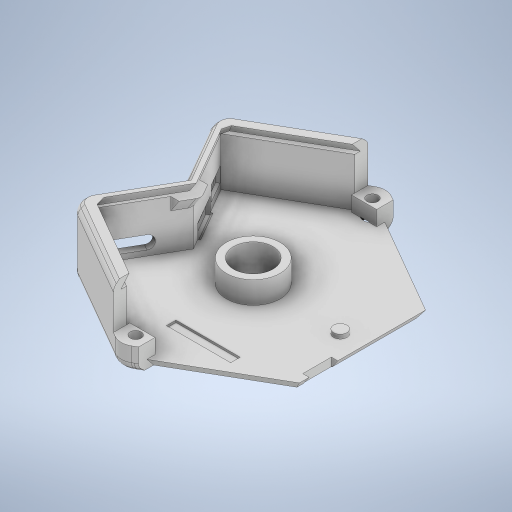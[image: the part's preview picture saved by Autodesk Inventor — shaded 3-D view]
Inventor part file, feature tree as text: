
AUTODESK INVENTOR PART (.ipt)
format: ipt  version: 2024 (Build 280153000, 153)  size: 1,035,776 bytes
history: native  units: in
note: dims shown in document units (in); Inventor stores cm internally (conversion verified against a paired STEP export)
features: extrude x31, move_body x17, direct_edit x9, draft x6, sketch x4, fillet x3, chamfer x3, plane x1
ambient origin geometry x8: Origin, YZ Plane, XZ Plane, XY Plane, X Axis, Y Axis, Z Axis, Center Point
bodies: Solid1 (feature_tree)
feature tree (74):
  extrude  "Extrusion1"  Depth=0.374in
  extrude  "Extrusion2"  Depth=0.0787in TaperAngle=0.0deg
  extrude  "Extrusion3"  Depth=0.6181in TaperAngle=0.0deg
  extrude  "Extrusion6"  Depth=0.0197in
  extrude  "Extrusion9"  Depth=0.0197in
  extrude  "Extrusion11"  Depth=0.0197in
  extrude  "Extrusion12"  Depth=0.0197in
  extrude  "Extrusion13"  TaperAngle=0.0deg  [1 undecoded]
  extrude  "Extrusion14"  Depth=0.0197in
  extrude  "Extrusion15"  Depth=0.0197in
  extrude  "Extrusion16"  Depth=0.0709in
  direct_edit  "Direct Edit2"
  direct_edit  "Direct Edit3"
  extrude  "Extrusion17"  Depth=0.0709in
  extrude  "Extrusion19"  Depth=0.0197in
  extrude  "Extrusion26"  Depth=0.0197in
  extrude  "Extrusion27"  TaperAngle=0.0deg  [1 undecoded]
  sketch  "Sketch19"  dims[d1=0.5098in d2=0.374in]
  extrude  "Extrusion28"  Depth=0.3937in TaperAngle=0.0deg
  extrude  "Extrusion29"  TaperAngle=0.0deg  [1 undecoded]
  draft  "FaceDraft1"
  draft  "FaceDraft2"
  draft  "FaceDraft4"
  sketch  "Sketch20"  dims[d3=0.4449in d7=0.0787in d8=0.0in]
  extrude  "Extrusion30"  Depth=0.3937in TaperAngle=0.0deg
  extrude  "Extrusion31"  Depth=0.0197in TaperAngle=0.0deg
  extrude  "Extrusion32"  Depth=0.0787in
  direct_edit  "Direct Edit5"
  plane  "Work Plane1"
  extrude  "Extrusion37"  Depth=0.0197in TaperAngle=0.0deg
  extrude  "Extrusion38"  Depth=0.0787in
  extrude  "Extrusion39"  Depth=0.0197in TaperAngle=0.0deg
  extrude  "Extrusion40"  Depth=0.0787in TaperAngle=0.0deg
  extrude  "Extrusion42"  TaperAngle=0.0deg  [1 undecoded]
  draft  "FaceDraft5"
  fillet  "Fillet1"  Radius=0.0787in
  draft  "FaceDraft6"
  chamfer  "Chamfer5"  [1 undecoded]
  fillet  "Fillet5"  Radius=0.2405in
  direct_edit  "Direct Edit8"
  direct_edit  "Direct Edit9"
  direct_edit  "Direct Edit10"
  extrude  "Extrusion43"  Depth=0.0787in
  direct_edit  "Direct Edit13"
  direct_edit  "Direct Edit14"
  direct_edit  "Direct Edit15"
  extrude  "Extrusion44"  TaperAngle=0.0deg  [1 undecoded]
  chamfer  "Chamfer6"  [1 undecoded]
  draft  "FaceDraft7"
  fillet  "Fillet6"  Radius=0.3937in
  extrude  "Extrusion45"  Depth=0.0787in
  sketch  "Sketch27"  dims[d21=0.1642in d22=0.1071in d23=0.1142in d24=0.2276in d25=0.1142in d26=0.0in d27=0.0in d38=0.1929in d40=0.1732in d42=0.0709in d43=0.0709in d44=0.6871in d45=0.6871in d46=0.0in d47=0.0in d51=0.3937in d52=0.0in d56=0.0in d57=0.0in d58=0.3937in d59=0.0in d60=0.3976in d61=0.0in d63=0.0787in d64=0.0689in d65=0.0in d66=0.0787in d67=0.0689in d68=0.0in d69=0.0in d70=0.0in d71=0.0787in d72=0.0in d73=0.0in d74=-0.0689in d80=0.0787in d81=0.0in d82=0.0in d85=0.2405in d86=0.0787in d87=0.0in d88=0.0in d118=0.0in d119=0.0in d120=0.3937in d121=0.0in d122=0.0787in d123=30.0deg d124=0.0in d125=0.0in d126=0.3937in d127=0.0in d128=0.2405in d129=-0.2405in d134=0.2405in d135=0.1693in d137=0.0827in d138=0.0in d139=0.0906in d140=0.0in d141=0.0984in d142=0.0in d144=120.0deg d148=0.1575in d154=90.0deg d160=0.1354in d161=0.1378in d179=0.126in d180=0.8268in d181=0.0394in d182=0.0in d183=0.1299in d184=0.1417in d185=0.3937in d186=0.0in d199=0.0in d200=0.0in d201=0.1417in d202=0.0984in d204=0.0394in d205=0.0in d207=120.0deg d211=0.0in d212=0.0in d213=30.0deg d214=-0.2061in d215=0.0492in d216=0.0787in d217=45.0deg d218=0.0787in d219=0.0157in d220=0.0118in d221=0.0in d222=0.0in d223=-0.0059in d224=0.1043in d226=0.0906in d228=0.0in d229=0.0in d230=0.0197in d231=0.0in d232=0.0in d233=-0.0197in d234=0.1535in d235=0.0079in d236=0.1535in d237=0.0906in d239=0.1043in d240=0.0079in d241=0.0295in d242=0.0433in d243=0.0315in d244=0.0335in d247=0.9695in d248=120.0deg d249=0.0295in d250=0.0433in d251=0.065in d253=60.0deg d254=0.0in d255=0.0in d256=0.0157in d258=0.3779in d260=45.0deg d261=45.0deg d262=0.0in d263=0.0in d264=0.0098in d265=0.0in d266=0.0in d267=0.0098in d268=0.1043in d269=0.3937in d270=0.0in d277=0.2224in d278=0.0in d279=0.0in d280=0.0079in d281=0.0in d282=0.0in d283=0.0079in d284=0.0in d285=0.0in d286=0.0059in d287=0.0in d288=0.0in d289=0.0059in d290=0.0in d291=0.0in d292=-0.0039in d293=0.0in d294=0.0in d295=-0.0039in d296=0.0443in d297=0.0in d298=0.0in d299=-0.0079in d300=0.0in d301=0.0in d302=-0.0079in d303=0.0in d304=0.0in d305=-0.0059in d308=30.0deg d310=0.1181in d311=0.0in d312=0.0984in d313=0.0787in d314=45.0deg d315=0.0787in d316=30.0deg d317=0.0787in d318=0.1378in d319=0.2933in d320=0.0906in d321=0.0728in d322=0.6102in d323=0.0197in d324=0.0in d325=0.3937in d326=0.0in d327=0.3937in d328=0.0in d329=0.0394in d330=0.0394in d331=0.0197in d332=0.0197in d333=0.0315in d334=0.0in d335=0.0197in d336=0.0787in d337=45.0deg d33=0.0197in d34=0.0344in d35=0.0197in d36=0.0344in d62=0.0197in d112=0.0197in d113=0.0344in d114=0.0197in d115=0.0344in d131=0.0197in d132=0.0344in d133=0.0197in d136=0.0344in d166=0.0197in d167=0.0344in d168=0.0197in d169=0.0344in d210=0.0in d225=0.0197in d227=0.0197in]
  extrude  "Extrusion46"  TaperAngle=30.0deg  [1 undecoded]
  extrude  "Extrusion47"  TaperAngle=0.0deg  [1 undecoded]
  extrude  "Extrusion48"  Depth=0.3937in TaperAngle=0.0deg
  chamfer  "Chamfer7"  Distance=0.2405in
  sketch  "Sketch23"  dims[d9=0.2953in d10=0.0in d11=0.6181in d12=0.0in]
  move_body  "Move2"
  move_body  "Move3"
  move_body  "Move15"
  move_body  "Move16"
  move_body  "Move17"
  move_body  "Move18"
  move_body  "Move19"
  move_body  "Move20"
  move_body  "Move23"
  move_body  "Move24"
  move_body  "Move25"
  move_body  "Move26"
  move_body  "Move27"
  move_body  "Move28"
  move_body  "Move29"
  move_body  "Move30"
  move_body  "Move31"
note: 9 required parameter values undecoded (feature->parameter linkage not recoverable at this tier; creation-order binding heuristic only, values carry confidence <= 0.55)
